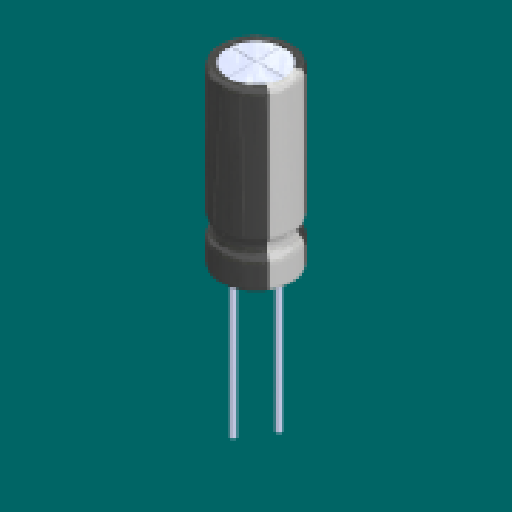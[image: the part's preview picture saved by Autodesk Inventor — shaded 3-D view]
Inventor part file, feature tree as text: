
AUTODESK INVENTOR PART (.ipt)
format: ipt  version: 2025.2 (Build 292293000, 293)  size: 185,856 bytes
history: native  units: mm
features: imported_body x5, extrude x2, sketch x2
ambient origin geometry x8: Origin, YZ Plane, XZ Plane, XY Plane, X Axis, Y Axis, Z Axis, Center Point
bodies: Solid1 (feature_tree), Solid2 (feature_tree), Solid3 (feature_tree), Solid4 (feature_tree), Solid5 (feature_tree)
feature tree (9):
  extrude  "Extrusion1"  Depth=9.25mm TaperAngle=0.0deg
  extrude  "Extrusion2"  [1 undecoded]
  sketch  "Sketch1"  dims[d0=9.25mm d1=0.0mm d2=9.25mm d3=0.0mm]
  sketch  "Sketch2"
  imported_body  "Base1"
  imported_body  "Base2"
  imported_body  "Base3"
  imported_body  "Base4"
  imported_body  "Base5"
note: 1 required parameter value undecoded (feature->parameter linkage not recoverable at this tier; creation-order binding heuristic only, values carry confidence <= 0.55)
